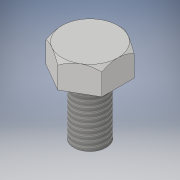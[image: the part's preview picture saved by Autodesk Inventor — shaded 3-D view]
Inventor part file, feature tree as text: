
AUTODESK INVENTOR PART (.ipt)
format: ipt  version: 2019 (Build 230136000, 136)  size: 126,464 bytes
history: native  units: in
note: dims shown in document units (in); Inventor stores cm internally (conversion verified against a paired STEP export)
features: extrude x3, sketch x3, thread x1
ambient origin geometry x8: Origin, YZ Plane, XZ Plane, XY Plane, X Axis, Y Axis, Z Axis, Center Point
bodies: Solid1 (feature_tree)
feature tree (7):
  extrude  "Extrusion1"  Depth=0.4in TaperAngle=0.0deg
  extrude  "Extrusion2"  Depth=0.4in
  extrude  "Extrusion3"  Depth=0.9in TaperAngle=0.0deg
  thread  "Thread1"  [1 undecoded]
  sketch  "Sketch1"  dims[d0=1.0in d1=0.4in d2=0.0in]
  sketch  "Sketch2"  dims[d3=0.4in d4=45.0deg d5=0.5in]
  sketch  "Sketch3"  dims[d6=0.9in d7=0.0in d8=1.0in d9=0.0in]
note: 1 required parameter value undecoded (feature->parameter linkage not recoverable at this tier; creation-order binding heuristic only, values carry confidence <= 0.55)
